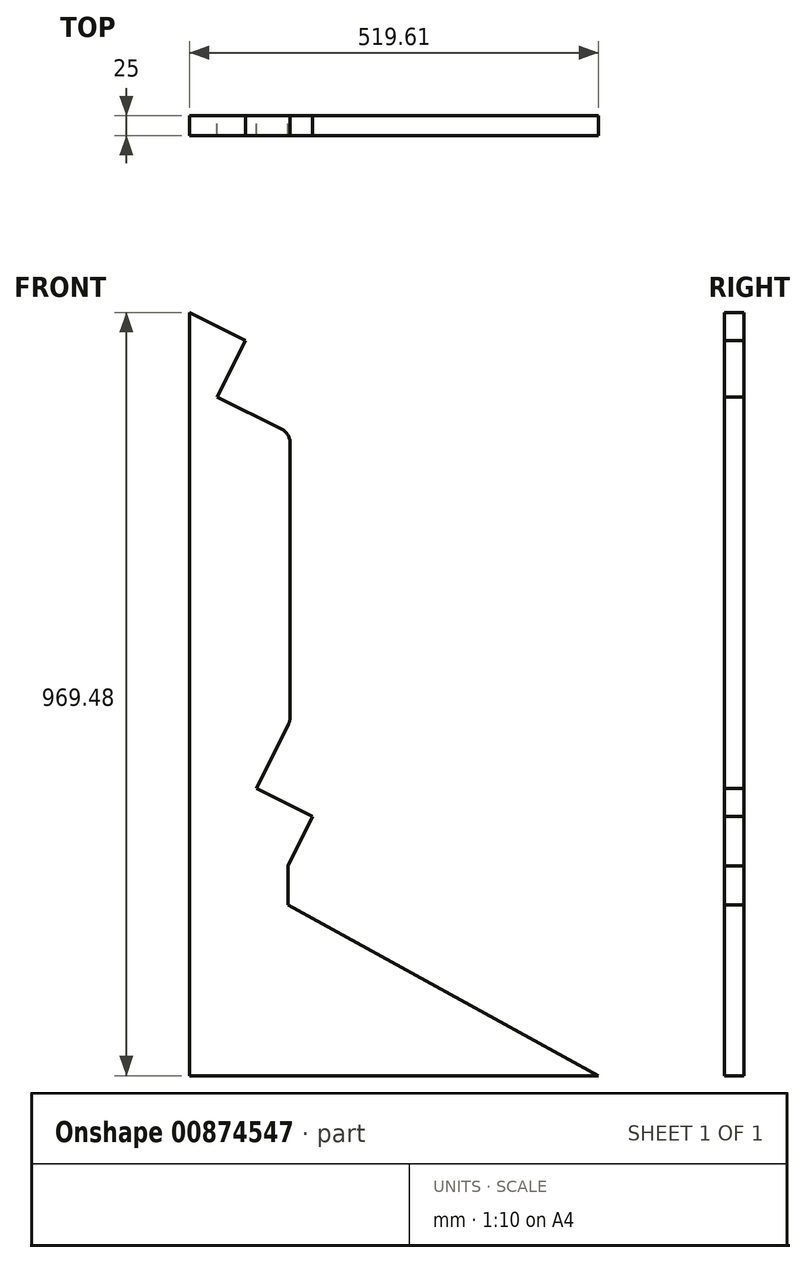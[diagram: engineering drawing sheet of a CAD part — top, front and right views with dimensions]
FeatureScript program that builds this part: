
annotation { "Feature Type Name" : "Feature", "Feature Type Description" : "" }
export const myFeature = defineFeature(function(context is Context, id is Id, definition is map)
    precondition{}
    {
        {
            var Q0;
            Q0=qCreatedBy(makeId("Front.planeOp"),FACE);
            var sketch = newSketch(context, id + "F0", { "sketchPlane" : qUnion([Q0])});
            skLineSegment(sketch, "E0", {"start": v(395.04, -610.83) * mm, "end": v(0.6, -394.21) * mm});
            skLineSegment(sketch, "E1", {"start": v(0.6, -394.21) * mm, "end": v(0.6, -344.21) * mm});
            skLineSegment(sketch, "E2", {"start": v(0.6, -344.21) * mm, "end": v(31.97, -281.63) * mm});
            skLineSegment(sketch, "E3", {"start": v(83.5, -155.17) * mm, "end": v(83.5, 192.6) * mm, "construction": true});
            skLineSegment(sketch, "E4", {"start": v(28.32, 281.98) * mm, "end": v(-8.58, 300.48) * mm, "construction": true});
            skPoint(sketch, "E5.visualSharp", {"position": v(83.5, 254.32) * mm});
            skArc(sketch, "E5.filletArc", {"start": v(83.5, 192.6) * mm, "mid": v(68.6, 245.12) * mm, "end": v(28.32, 281.98) * mm, "construction": true});
            skPoint(sketch, "E6.visualSharp", {"position": v(83.5, -178.82) * mm});
            skArc(sketch, "E6.filletArc", {"start": v(72.9, -199.97) * mm, "mid": v(80.81, -178.19) * mm, "end": v(83.5, -155.17) * mm, "construction": true});
            skLineSegment(sketch, "E7", {"start": v(-162.07, 359.65) * mm, "end": v(-162.07, -610.83) * mm, "construction": true});
            skLineSegment(sketch, "E8", {"start": v(-124.57, -610.83) * mm, "end": v(395.04, -610.83) * mm});
            skLineSegment(sketch, "E9.0", {"start": v(14.87, 255.17) * mm, "end": v(-22.02, 273.67) * mm, "construction": true});
            skLineSegment(sketch, "E9.1", {"start": v(27.55, -223.5) * mm, "end": v(46.08, -186.53) * mm, "construction": true});
            skArc(sketch, "E9.2", {"start": v(46.08, -186.53) * mm, "mid": v(51.62, -171.28) * mm, "end": v(53.5, -155.17) * mm, "construction": true});
            skLineSegment(sketch, "E9.3", {"start": v(53.5, -155.17) * mm, "end": v(53.5, 192.6) * mm, "construction": true});
            skArc(sketch, "E9.4", {"start": v(53.5, 192.6) * mm, "mid": v(43.06, 229.36) * mm, "end": v(14.87, 255.17) * mm, "construction": true});
            skLineSegment(sketch, "E10", {"start": v(-8.58, 300.48) * mm, "end": v(-22.02, 273.67) * mm, "construction": true});
            skLineSegment(sketch, "E11.0", {"start": v(31.97, -281.63) * mm, "end": v(-39.55, -245.79) * mm});
            skLineSegment(sketch, "E11.1", {"start": v(-39.55, -245.79) * mm, "end": v(1.38, -164.13) * mm});
            skArc(sketch, "E11.2", {"start": v(1.38, -164.13) * mm, "mid": v(2.96, -159.77) * mm, "end": v(3.5, -155.17) * mm});
            skLineSegment(sketch, "E11.3", {"start": v(-53.27, 322.9) * mm, "end": v(-89.13, 251.38) * mm});
            skLineSegment(sketch, "E11.4", {"start": v(-7.54, 210.47) * mm, "end": v(-89.13, 251.38) * mm});
            skArc(sketch, "E11.5", {"start": v(3.5, 192.6) * mm, "mid": v(0.52, 203.1) * mm, "end": v(-7.54, 210.47) * mm});
            skLineSegment(sketch, "E11.6", {"start": v(3.5, -155.17) * mm, "end": v(3.5, 192.6) * mm});
            skLineSegment(sketch, "E12.trimOffspring", {"start": v(-53.27, 322.9) * mm, "end": v(-126.57, 359.65) * mm});
            skLineSegment(sketch, "E13.trimOffspring", {"start": v(54.37, -236.93) * mm, "end": v(72.9, -199.97) * mm, "construction": true});
            skLineSegment(sketch, "E14.0", {"start": v(-124.57, 359.65) * mm, "end": v(-124.57, -610.83) * mm});
            skSolve(sketch);
        }
        {
            var Q0;
            Q0=makeQuery(id+"F0.imprint","IMPRINT",FACE,{"disambiguationData":[TD([[makeQuery(id+"F0.imprint","IMPRINT",EDGE,{"derivedFrom":sQuery(id+"F0.wireOp",EDGE,"E0")}),1.0]])]});
            extrude(context, id + "F1", {"entities" : qUnion([Q0]), "depth" : 25 * mm, "offsetDistance" : 25 * mm});
        }
    });
